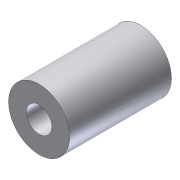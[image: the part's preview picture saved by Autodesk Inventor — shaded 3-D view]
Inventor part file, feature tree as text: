
AUTODESK INVENTOR PART (.ipt)
format: ipt  version: 2012 (Build 160160000, 160)  size: 81,920 bytes
history: native  units: in
note: dims shown in document units (in); Inventor stores cm internally (conversion verified against a paired STEP export)
features: extrude x1, sketch x1
ambient origin geometry x8: Origin, YZ Plane, XZ Plane, XY Plane, X Axis, Y Axis, Z Axis, Center Point
bodies: Solid1 (feature_tree)
feature tree (2):
  extrude  "Extrusion1"  Depth=1.5in
  sketch  "Sketch1"  dims[d0=0.625in d1=1.5in d2=2.5in d3=0.0in]
